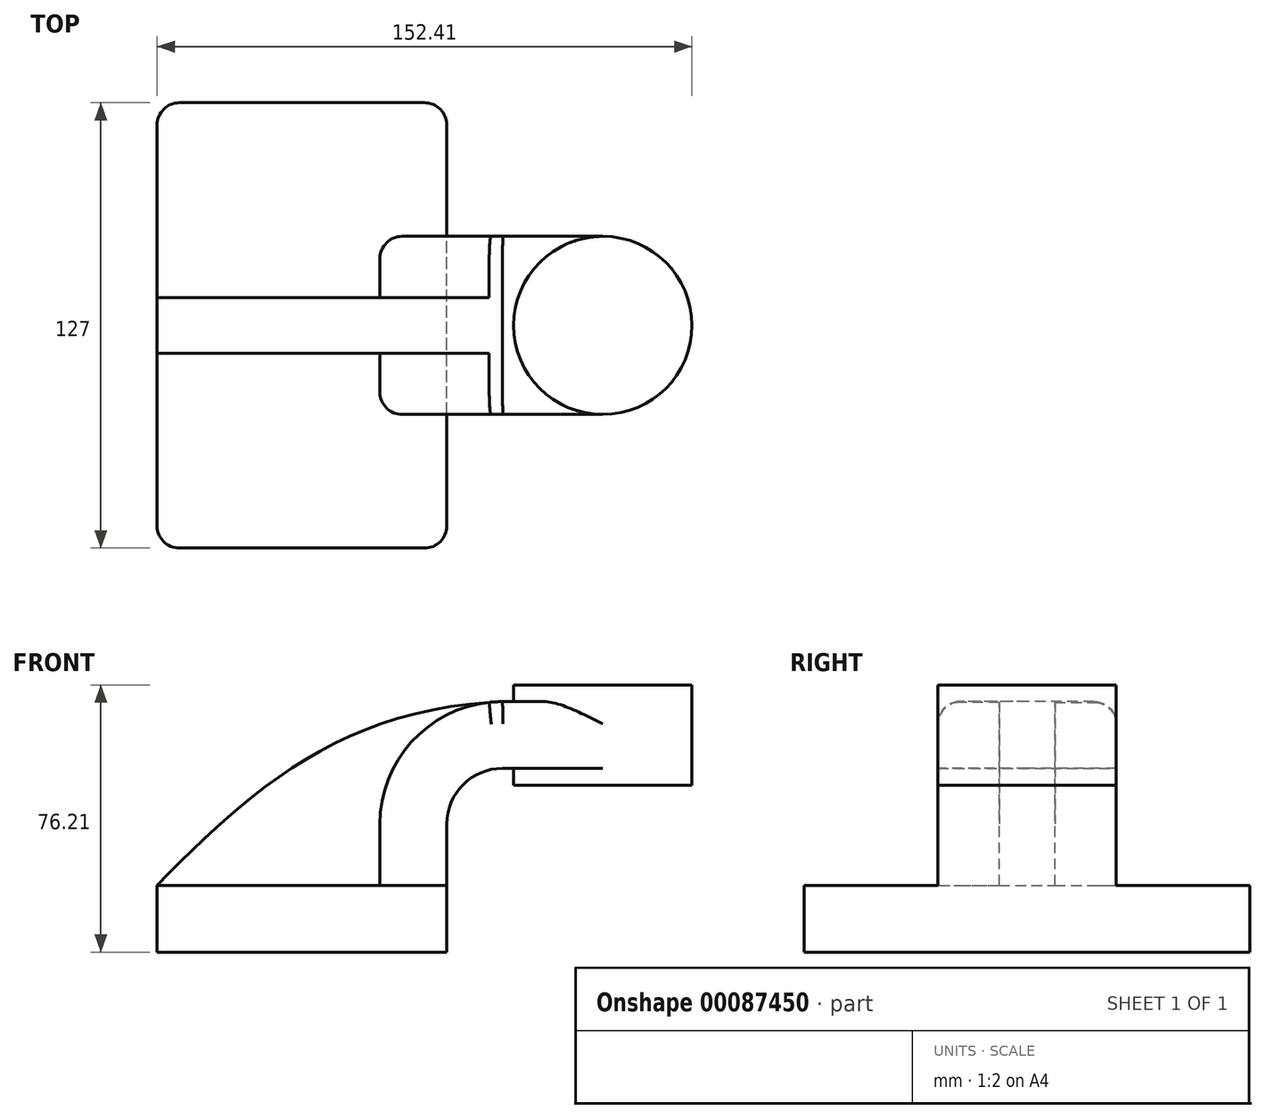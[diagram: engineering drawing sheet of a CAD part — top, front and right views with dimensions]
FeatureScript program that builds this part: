
annotation { "Feature Type Name" : "Feature", "Feature Type Description" : "" }
export const myFeature = defineFeature(function(context is Context, id is Id, definition is map)
    precondition{}
    {
        {
            var Q0;
            Q0=qCreatedBy(makeId("Front.planeOp"),FACE);
            var sketch = newSketch(context, id + "F0", { "sketchPlane" : qUnion([Q0])});
            skLineSegment(sketch, "E0.bottom", {"start": v(41.28, -9.52) * mm, "end": v(-41.28, -9.53) * mm});
            skLineSegment(sketch, "E0.top", {"start": v(41.28, 9.53) * mm, "end": v(-41.28, 9.53) * mm});
            skLineSegment(sketch, "E0.left", {"start": v(41.28, -9.52) * mm, "end": v(41.28, 9.53) * mm});
            skLineSegment(sketch, "E0.right", {"start": v(-41.28, -9.53) * mm, "end": v(-41.28, 9.53) * mm});
            skPoint(sketch, "E0.middle", {"position": v(0, 0) * mm});
            skLineSegment(sketch, "E1.bottom", {"start": v(111.12, 38.1) * mm, "end": v(60.33, 38.1) * mm});
            skLineSegment(sketch, "E1.top", {"start": v(111.12, 66.68) * mm, "end": v(60.33, 66.68) * mm});
            skLineSegment(sketch, "E1.left", {"start": v(111.12, 38.1) * mm, "end": v(111.12, 66.68) * mm});
            skLineSegment(sketch, "E1.right", {"start": v(60.33, 38.1) * mm, "end": v(60.33, 66.68) * mm});
            skPoint(sketch, "E1.middle", {"position": v(85.72, 52.39) * mm});
            skLineSegment(sketch, "E2", {"start": v(41.28, 9.53) * mm, "end": v(41.28, 27) * mm});
            skArc(sketch, "E3", {"start": v(41.27, 27) * mm, "mid": v(45.92, 38.23) * mm, "end": v(57.15, 42.88) * mm});
            skLineSegment(sketch, "E4", {"start": v(57.15, 42.88) * mm, "end": v(85.72, 42.88) * mm});
            skLineSegment(sketch, "E5.0", {"start": v(57.15, 61.93) * mm, "end": v(85.72, 61.93) * mm});
            skArc(sketch, "E5.1", {"start": v(22.23, 27) * mm, "mid": v(32.45, 51.7) * mm, "end": v(57.15, 61.93) * mm});
            skLineSegment(sketch, "E5.2", {"start": v(22.22, 9.53) * mm, "end": v(22.22, 27) * mm});
            skLineSegment(sketch, "E6", {"start": v(85.72, 38.1) * mm, "end": v(85.72, 66.68) * mm});
            skFitSpline(sketch, "E7", {"points": [v(-41.28, 9.52) * mm, v(57.15, 61.93) * mm], "startDerivative": vector(77.95, 79.83) * mm, "endDerivative": vector(138.35, 5.62) * mm});
            skSolve(sketch);
        }
        {
            var Q0;
            Q0=makeQuery(id+"F0.imprint","IMPRINT",FACE,{"disambiguationData":[TD([[makeQuery(id+"F0.imprint","IMPRINT",EDGE,{"derivedFrom":sQuery(id+"F0.wireOp",EDGE,"E0.bottom")}),-1.0]])]});
            extrude(context, id + "F1", {"entities" : qUnion([Q0]), "endBound" : BoundingType.SYMMETRIC, "depth" : 127 * mm});
        }
        {
            var Q0;
            {var subQ1=sQuery(id+"F0.wireOp",EDGE,"E2");Q0=makeQuery(id+"F0.imprint","IMPRINT",FACE,{"disambiguationData":[TD([[makeQuery(id+"F0.imprint","IMPRINT",EDGE,{"derivedFrom":subQ1}),1.0]])]});}
            var Q1;
            {var subQ0=sQuery(id+"F0.wireOp",EDGE,"E4");var subQ1=sQuery(id+"F0.wireOp",EDGE,"E1.right");var subQ2=makeQuery(id+"F0.imprint","INTERSECT",VERTEX,{"derivedFrom":[subQ1,subQ0]});Q1=makeQuery(id+"F0.imprint","IMPRINT",FACE,{"disambiguationData":[TD([[makeQuery(id+"F0.imprint","IMPRINT",EDGE,{"disambiguationData":[TD([[subQ2,-1.0]])],"derivedFrom":subQ1}),-1.0]])]});}
            extrude(context, id + "F2", {"entities" : qUnion([Q0, Q1]), "operationType" : NewBodyOperationType.ADD, "endBound" : BoundingType.SYMMETRIC, "depth" : 50.8 * mm});
        }
        {
            var Q0;
            {var subQ3=sQuery(id+"F0.wireOp",EDGE,"E5.2");Q0=makeQuery(id+"F0.imprint","IMPRINT",FACE,{"disambiguationData":[TD([[makeQuery(id+"F0.imprint","IMPRINT",EDGE,{"derivedFrom":subQ3}),1.0]])]});}
            extrude(context, id + "F3", {"entities" : qUnion([Q0]), "operationType" : NewBodyOperationType.ADD, "endBound" : BoundingType.SYMMETRIC, "depth" : 15.88 * mm});
        }
        {
            var Q0;
            {var subQ0=sQuery(id+"F0.wireOp",EDGE,"E1.left");Q0=makeQuery(id+"F0.imprint","IMPRINT",FACE,{"disambiguationData":[TD([[makeQuery(id+"F0.imprint","IMPRINT",EDGE,{"derivedFrom":subQ0}),1.0]])]});}
            var Q1;
            Q1=sQuery(id+"F0.wireOp",EDGE,"E6");
            revolve(context, id + "F4", {"operationType" : NewBodyOperationType.ADD, "entities" : qUnion([Q0]), "axis" : qUnion([Q1]), "revolveType" : RevolveType.FULL});
        }
        {
            var Q0;
            Q0=makeQuery(id+"F1.opExtrude","CAP_EDGE",EDGE,{"disambiguationData":[OSD([sQuery(id+"F0.wireOp",EDGE,"E0.left")])],"isStart":false});
            var Q1;
            Q1=makeQuery(id+"F1.opExtrude","CAP_EDGE",EDGE,{"disambiguationData":[OSD([sQuery(id+"F0.wireOp",EDGE,"E0.right")])],"isStart":false});
            var Q2;
            Q2=makeQuery(id+"F1.opExtrude","CAP_EDGE",EDGE,{"disambiguationData":[OSD([sQuery(id+"F0.wireOp",EDGE,"E0.left")])],"isStart":true});
            var Q3;
            Q3=makeQuery(id+"F1.opExtrude","CAP_EDGE",EDGE,{"disambiguationData":[OSD([sQuery(id+"F0.wireOp",EDGE,"E0.right")])],"isStart":true});
            fillet(context, id + "F5", {"entities" : qUnion([Q0, Q1, Q2, Q3]), "radius" : 6.35 * mm, "tangentPropagation" : true, "allowEdgeOverflow" : false});
        }
        {
            var Q0;
            Q0=makeQuery(id+"F2.opExtrude","CAP_EDGE",EDGE,{"disambiguationData":[OSD([sQuery(id+"F0.wireOp",EDGE,"E5.1")])],"isStart":true});
            var Q1;
            Q1=makeQuery(id+"F2.opExtrude","CAP_EDGE",EDGE,{"disambiguationData":[OSD([sQuery(id+"F0.wireOp",EDGE,"E5.2")])],"isStart":true});
            var Q2;
            Q2=makeQuery(id+"F2.opExtrude","CAP_EDGE",EDGE,{"disambiguationData":[OSD([sQuery(id+"F0.wireOp",EDGE,"E5.0")])],"isStart":true});
            var Q3;
            Q3=makeQuery(id+"F2.opExtrude","CAP_EDGE",EDGE,{"disambiguationData":[OSD([sQuery(id+"F0.wireOp",EDGE,"E7")])],"isStart":true});
            var Q4;
            Q4=makeQuery(id+"F2.opExtrude","CAP_EDGE",EDGE,{"disambiguationData":[OSD([sQuery(id+"F0.wireOp",EDGE,"E5.0")])],"isStart":false});
            var Q5;
            Q5=makeQuery(id+"F2.opExtrude","CAP_EDGE",EDGE,{"disambiguationData":[OSD([sQuery(id+"F0.wireOp",EDGE,"E7")])],"isStart":false});
            var Q6;
            Q6=makeQuery(id+"F2.opExtrude","CAP_EDGE",EDGE,{"disambiguationData":[OSD([sQuery(id+"F0.wireOp",EDGE,"E5.1")])],"isStart":false});
            fillet(context, id + "F6", {"entities" : qUnion([Q0, Q1, Q2, Q3, Q4, Q5, Q6]), "radius" : 6.35 * mm, "tangentPropagation" : true, "allowEdgeOverflow" : false});
        }
    });
